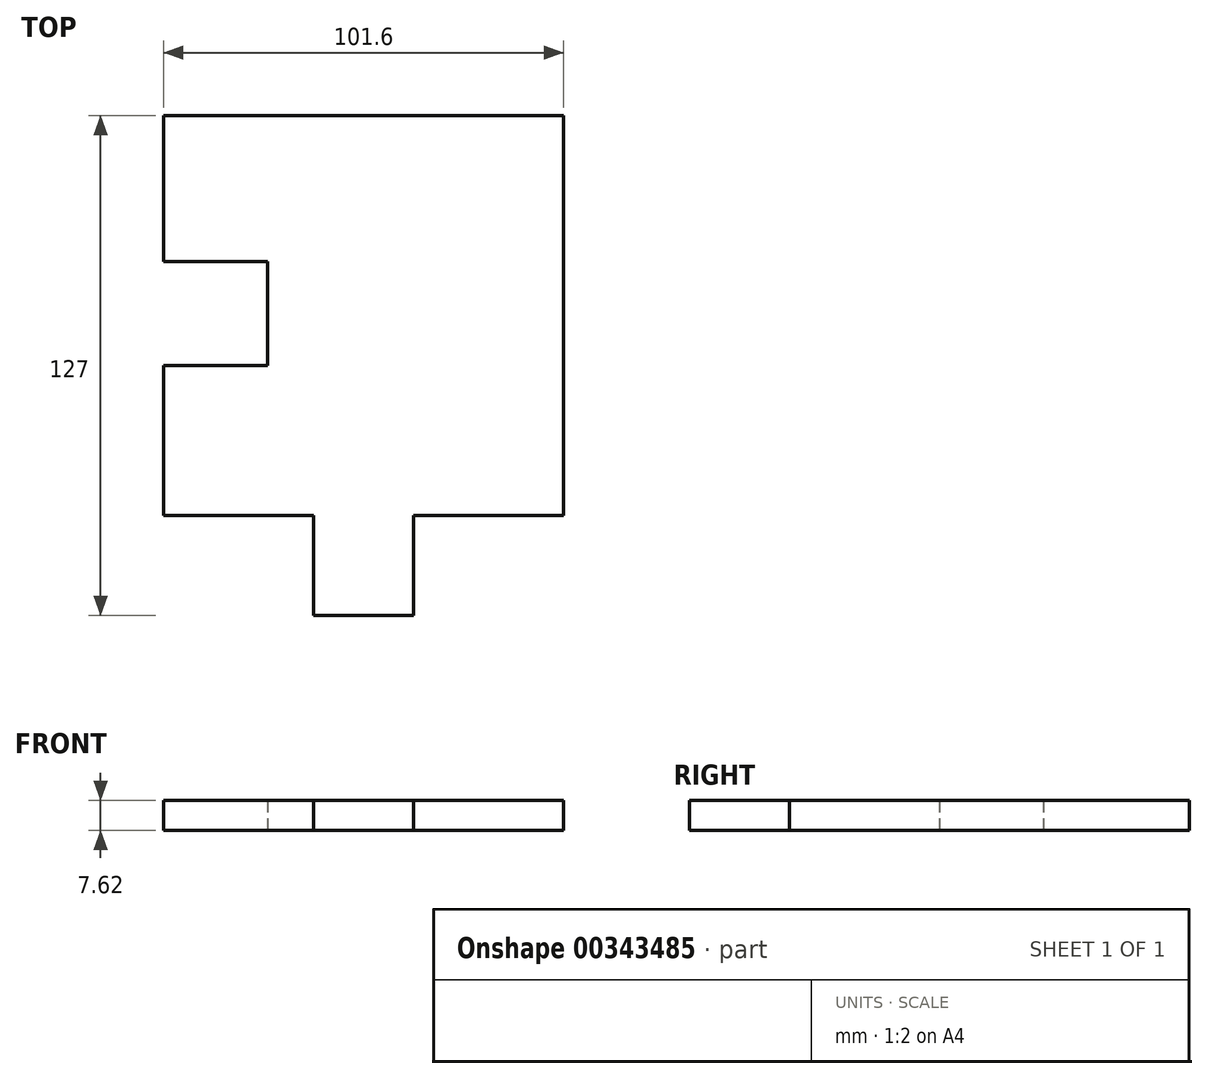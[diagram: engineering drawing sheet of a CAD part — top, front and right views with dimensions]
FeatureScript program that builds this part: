
annotation { "Feature Type Name" : "Feature", "Feature Type Description" : "" }
export const myFeature = defineFeature(function(context is Context, id is Id, definition is map)
    precondition{}
    {
        {
            var Q0;
            Q0=qCreatedBy(makeId("Top.planeOp"),FACE);
            var sketch = newSketch(context, id + "F0", { "sketchPlane" : qUnion([Q0])});
            skLineSegment(sketch, "E0.bottom", {"start": v(50.8, -50.8) * mm, "end": v(-50.8, -50.8) * mm});
            skLineSegment(sketch, "E0.top", {"start": v(50.8, 50.8) * mm, "end": v(-50.8, 50.8) * mm});
            skLineSegment(sketch, "E0.left", {"start": v(50.8, -50.8) * mm, "end": v(50.8, 50.8) * mm});
            skLineSegment(sketch, "E0.right", {"start": v(-50.8, -50.8) * mm, "end": v(-50.8, -12.7) * mm});
            skPoint(sketch, "E0.middle", {"position": v(0, 0) * mm});
            skLineSegment(sketch, "E1", {"start": v(-12.7, -50.8) * mm, "end": v(-12.7, -76.2) * mm});
            skLineSegment(sketch, "E2", {"start": v(-12.7, -76.2) * mm, "end": v(12.7, -76.2) * mm});
            skLineSegment(sketch, "E3", {"start": v(12.7, -76.2) * mm, "end": v(12.7, -50.8) * mm});
            skLineSegment(sketch, "E4", {"start": v(-50.8, -12.7) * mm, "end": v(-24.38, -12.7) * mm});
            skLineSegment(sketch, "E5", {"start": v(-24.38, -12.7) * mm, "end": v(-24.38, 13.72) * mm});
            skLineSegment(sketch, "E6", {"start": v(-24.38, 13.72) * mm, "end": v(-50.8, 13.72) * mm});
            skLineSegment(sketch, "E7.trimOffspring", {"start": v(-50.8, 13.72) * mm, "end": v(-50.8, 50.8) * mm});
            skSolve(sketch);
        }
        {
            var Q0;
            Q0 = qSketchRegion(id + "F0", true);
            extrude(context, id + "F1", {"entities" : qUnion([Q0]), "depth" : 7.62 * mm});
        }
    });
